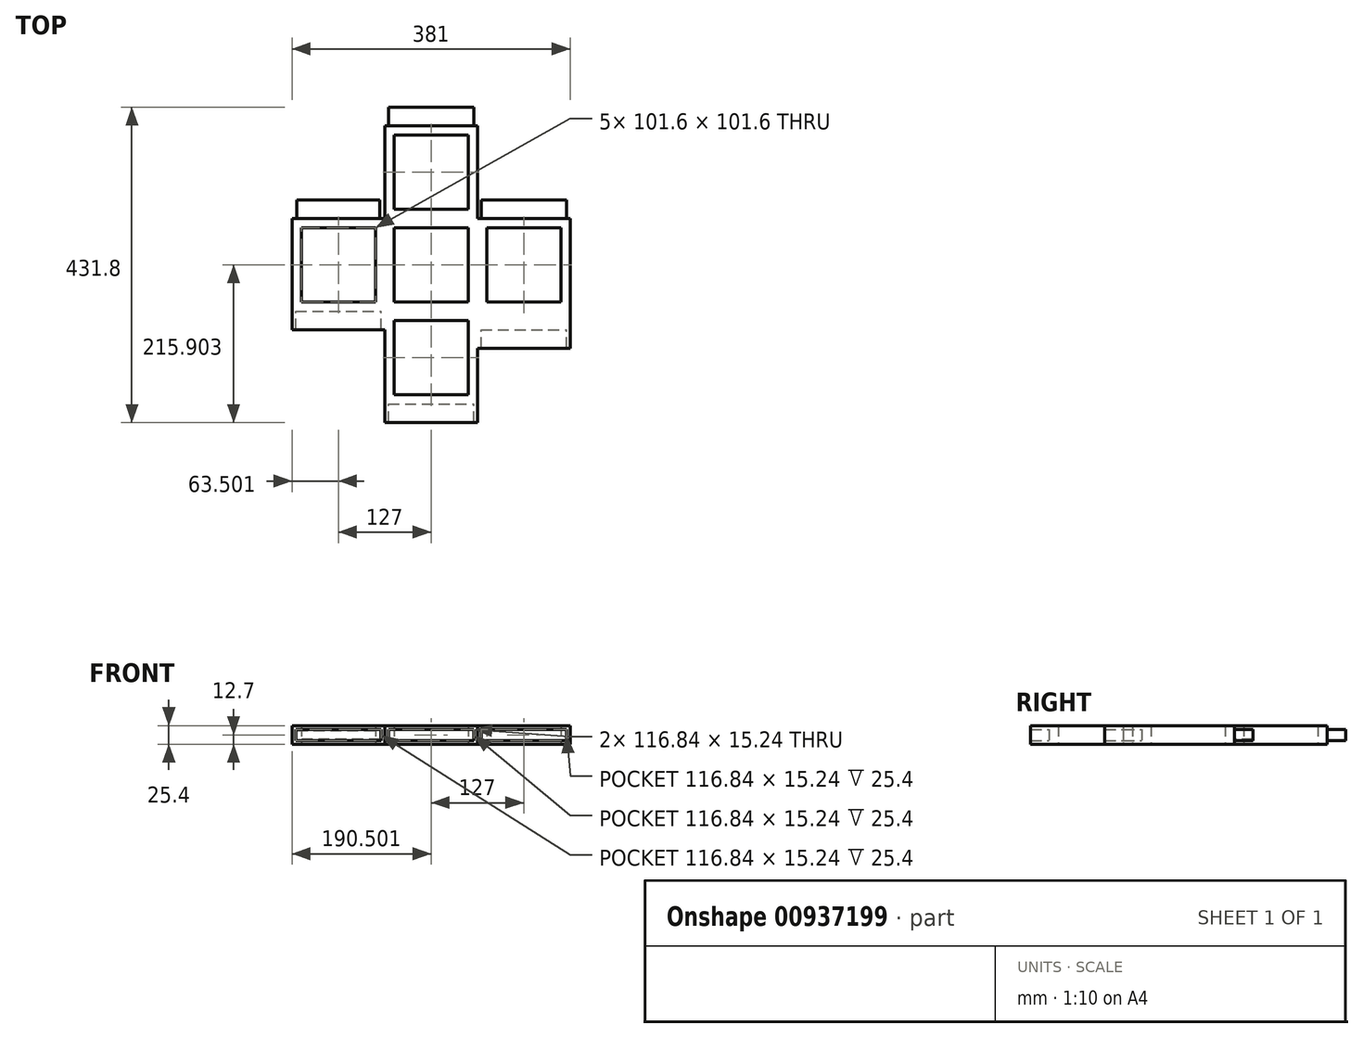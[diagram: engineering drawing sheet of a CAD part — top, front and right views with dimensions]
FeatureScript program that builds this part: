
annotation { "Feature Type Name" : "Feature", "Feature Type Description" : "" }
export const myFeature = defineFeature(function(context is Context, id is Id, definition is map)
    precondition{}
    {
        {
            var Q0;
            Q0=qCreatedBy(makeId("Top.planeOp"),FACE);
            var sketch = newSketch(context, id + "F0", { "sketchPlane" : qUnion([Q0])});
            skLineSegment(sketch, "E0.bottom", {"start": v(-63.69, 63.92) * mm, "end": v(63.31, 63.92) * mm});
            skLineSegment(sketch, "E0.top", {"start": v(-63.69, -63.08) * mm, "end": v(63.31, -63.08) * mm});
            skLineSegment(sketch, "E0.left", {"start": v(-63.69, 63.92) * mm, "end": v(-63.69, -63.08) * mm});
            skLineSegment(sketch, "E0.right", {"start": v(63.31, 63.92) * mm, "end": v(63.31, -63.08) * mm});
            skPoint(sketch, "E1", {"position": v(0, 0) * mm});
            skLineSegment(sketch, "E2", {"start": v(-63.69, 63.92) * mm, "end": v(63.31, -63.08) * mm, "construction": true});
            skLineSegment(sketch, "E3", {"start": v(63.31, 63.92) * mm, "end": v(-63.69, -63.08) * mm, "construction": true});
            skLineSegment(sketch, "E4.0", {"start": v(-50.99, 51.22) * mm, "end": v(50.61, 51.22) * mm});
            skLineSegment(sketch, "E4.1", {"start": v(-50.99, 51.22) * mm, "end": v(-50.99, -50.38) * mm});
            skLineSegment(sketch, "E4.2", {"start": v(-50.99, -50.38) * mm, "end": v(50.61, -50.38) * mm});
            skLineSegment(sketch, "E4.3", {"start": v(50.61, 51.22) * mm, "end": v(50.61, -50.38) * mm});
            skPoint(sketch, "E5.MirrorP", {"position": v(126.62, 0) * mm});
            skLineSegment(sketch, "E6.MirrorCS", {"start": v(190.31, 63.92) * mm, "end": v(190.31, -63.08) * mm});
            skLineSegment(sketch, "E7.MirrorCS", {"start": v(177.61, 51.22) * mm, "end": v(76.01, 51.22) * mm});
            skLineSegment(sketch, "E8.MirrorCS", {"start": v(76.01, 51.22) * mm, "end": v(76.01, -50.38) * mm});
            skLineSegment(sketch, "E9.MirrorCS", {"start": v(177.61, 51.22) * mm, "end": v(177.61, -50.38) * mm});
            skLineSegment(sketch, "E10.MirrorCS", {"start": v(177.61, -50.38) * mm, "end": v(76.01, -50.38) * mm});
            skLineSegment(sketch, "E11.MirrorCS", {"start": v(190.31, -63.08) * mm, "end": v(63.31, -63.08) * mm});
            skPoint(sketch, "E12.MirrorP", {"position": v(0, -126.15) * mm});
            skLineSegment(sketch, "E13.MirrorCS", {"start": v(50.61, -177.38) * mm, "end": v(50.61, -75.78) * mm});
            skLineSegment(sketch, "E14.MirrorCS", {"start": v(-50.99, -75.78) * mm, "end": v(50.61, -75.78) * mm});
            skLineSegment(sketch, "E15.MirrorCS", {"start": v(-50.99, -177.38) * mm, "end": v(-50.99, -75.78) * mm});
            skLineSegment(sketch, "E16.MirrorCS", {"start": v(-50.99, -177.38) * mm, "end": v(50.61, -177.38) * mm});
            skPoint(sketch, "E17.MirrorP", {"position": v(-127.38, 0) * mm});
            skLineSegment(sketch, "E18.MirrorCS", {"start": v(-76.39, 51.22) * mm, "end": v(-76.39, -50.38) * mm});
            skLineSegment(sketch, "E19.MirrorCS", {"start": v(-177.99, 51.22) * mm, "end": v(-177.99, -50.38) * mm});
            skLineSegment(sketch, "E20.MirrorCS", {"start": v(-76.39, -50.38) * mm, "end": v(-177.99, -50.38) * mm});
            skLineSegment(sketch, "E21.MirrorCS", {"start": v(-76.39, 51.22) * mm, "end": v(-177.99, 51.22) * mm});
            skLineSegment(sketch, "E22.MirrorCS", {"start": v(-63.69, 63.92) * mm, "end": v(-190.69, 63.92) * mm});
            skPoint(sketch, "E23.MirrorP", {"position": v(0, 127.85) * mm});
            skLineSegment(sketch, "E24.MirrorCS", {"start": v(50.61, 76.62) * mm, "end": v(50.61, 178.22) * mm});
            skLineSegment(sketch, "E25.MirrorCS", {"start": v(-50.99, 76.62) * mm, "end": v(-50.99, 178.22) * mm});
            skLineSegment(sketch, "E26.MirrorCS", {"start": v(-50.99, 178.22) * mm, "end": v(50.61, 178.22) * mm});
            skLineSegment(sketch, "E27.MirrorCS", {"start": v(-50.99, 76.62) * mm, "end": v(50.61, 76.62) * mm});
            skLineSegment(sketch, "E28", {"start": v(-190.69, 63.92) * mm, "end": v(-190.69, -63.08) * mm});
            skLineSegment(sketch, "E29", {"start": v(-63.69, -63.08) * mm, "end": v(-190.69, -63.08) * mm});
            skLineSegment(sketch, "E30", {"start": v(63.31, 63.92) * mm, "end": v(190.31, 63.92) * mm});
            skLineSegment(sketch, "E31", {"start": v(-63.69, -63.08) * mm, "end": v(-63.69, -190.08) * mm});
            skLineSegment(sketch, "E32", {"start": v(63.31, -190.08) * mm, "end": v(-63.69, -190.08) * mm});
            skLineSegment(sketch, "E33", {"start": v(63.31, -190.08) * mm, "end": v(63.31, -63.08) * mm});
            skLineSegment(sketch, "E34", {"start": v(-63.69, 63.92) * mm, "end": v(-63.69, 190.92) * mm});
            skLineSegment(sketch, "E35", {"start": v(63.31, 190.92) * mm, "end": v(-63.69, 190.92) * mm});
            skLineSegment(sketch, "E36", {"start": v(63.31, 190.92) * mm, "end": v(63.31, 63.92) * mm});
            skSolve(sketch);
        }
        {
            var Q0;
            Q0 = qSketchRegion(id + "F0", true);
            extrude(context, id + "F1", {"entities" : qUnion([Q0]), "depth" : 25.4 * mm, "offsetDistance" : 25.4 * mm});
        }
        {
            var Q0;
            Q0=makeQuery(id+"F1.opExtrude","SWEPT_FACE",FACE,{"disambiguationData":[OSD([sQuery(id+"F0.wireOp",EDGE,"E35")])]});
            var sketch = newSketch(context, id + "F2", { "sketchPlane" : qUnion([Q0])});
            skLineSegment(sketch, "E37.0", {"start": v(-58.23, 5.08) * mm, "end": v(58.6, 5.08) * mm});
            skLineSegment(sketch, "E37.1", {"start": v(-58.23, 20.32) * mm, "end": v(-58.23, 5.08) * mm});
            skLineSegment(sketch, "E37.2", {"start": v(58.6, 20.32) * mm, "end": v(-58.23, 20.32) * mm});
            skLineSegment(sketch, "E37.3", {"start": v(58.6, 5.08) * mm, "end": v(58.6, 20.32) * mm});
            skLineSegment(sketch, "E38.0", {"start": v(-63.31, 20.32) * mm, "end": v(-63.31, 5.08) * mm});
            skSolve(sketch);
        }
        {
            var Q0;
            Q0=makeQuery(id+"F2.imprint","IMPRINT",FACE,{"disambiguationData":[TD([[makeQuery(id+"F2.imprint","IMPRINT",EDGE,{"derivedFrom":sQuery(id+"F2.wireOp",EDGE,"E37.0")}),1.0]])]});
            extrude(context, id + "F3", {"entities" : qUnion([Q0]), "operationType" : NewBodyOperationType.ADD, "depth" : 25.4 * mm, "offsetDistance" : 25.4 * mm});
        }
        {
            var Q0;
            Q0=makeQuery(id+"F1.opExtrude","SWEPT_FACE",FACE,{"disambiguationData":[OSD([sQuery(id+"F0.wireOp",EDGE,"E22.MirrorCS")])]});
            var sketch = newSketch(context, id + "F4", { "sketchPlane" : qUnion([Q0])});
            skSolve(sketch);
        }
        {
            var Q0;
            {var subQ0=sQuery(id+"F0.wireOp",EDGE,"E22.MirrorCS");Q0=makeQuery(id+"F4.imprint","IMPRINT",FACE,{"disambiguationData":[TD([[makeQuery(id+"F4.imprint","IMPRINT",EDGE,{"derivedFrom":makeQuery(id+"F1.opExtrude","CAP_EDGE",EDGE,{"disambiguationData":[OSD([subQ0])],"isStart":true})}),1.0]])]});}
            var sketch = newSketch(context, id + "F5", { "sketchPlane" : qUnion([Q0])});
            skLineSegment(sketch, "E39.0", {"start": v(70.35, 18.74) * mm, "end": v(70.35, 6.66) * mm});
            skLineSegment(sketch, "E39.1", {"start": v(184.03, 18.74) * mm, "end": v(70.35, 18.74) * mm});
            skLineSegment(sketch, "E39.2", {"start": v(184.03, 6.66) * mm, "end": v(184.03, 18.74) * mm});
            skLineSegment(sketch, "E39.3", {"start": v(70.35, 6.66) * mm, "end": v(184.03, 6.66) * mm});
            skSolve(sketch);
        }
        {
            var Q0;
            Q0=makeQuery(id+"F5.imprint","IMPRINT",FACE,{"disambiguationData":[TD([[makeQuery(id+"F5.imprint","IMPRINT",EDGE,{"derivedFrom":sQuery(id+"F5.wireOp",EDGE,"E39.0")}),1.0]])]});
            extrude(context, id + "F6", {"entities" : qUnion([Q0]), "operationType" : NewBodyOperationType.ADD, "depth" : 25.4 * mm, "offsetDistance" : 25.4 * mm});
        }
        {
            var Q0;
            Q0=makeQuery(id+"F1.opExtrude","SWEPT_FACE",FACE,{"disambiguationData":[OSD([sQuery(id+"F0.wireOp",EDGE,"E30")])]});
            var sketch = newSketch(context, id + "F7", { "sketchPlane" : qUnion([Q0])});
            skLineSegment(sketch, "E40.0", {"start": v(-185.23, 5.08) * mm, "end": v(-68.4, 5.08) * mm});
            skLineSegment(sketch, "E40.1", {"start": v(-185.23, 20.32) * mm, "end": v(-185.23, 5.08) * mm});
            skLineSegment(sketch, "E40.2", {"start": v(-68.4, 20.32) * mm, "end": v(-185.23, 20.32) * mm});
            skLineSegment(sketch, "E40.3", {"start": v(-68.4, 5.08) * mm, "end": v(-68.4, 20.32) * mm});
            skLineSegment(sketch, "E41.0", {"start": v(-180.15, 20.32) * mm, "end": v(-180.15, 5.08) * mm});
            skSolve(sketch);
        }
        {
            var Q0;
            {var subQ0=sQuery(id+"F7.wireOp",EDGE,"E40.1");Q0=makeQuery(id+"F7.imprint","IMPRINT",FACE,{"disambiguationData":[TD([[makeQuery(id+"F7.imprint","IMPRINT",EDGE,{"derivedFrom":subQ0}),1.0]])]});}
            var Q1;
            {var subQ0=sQuery(id+"F7.wireOp",EDGE,"E40.3");Q1=makeQuery(id+"F7.imprint","IMPRINT",FACE,{"disambiguationData":[TD([[makeQuery(id+"F7.imprint","IMPRINT",EDGE,{"derivedFrom":subQ0}),1.0]])]});}
            extrude(context, id + "F8", {"entities" : qUnion([Q0, Q1]), "operationType" : NewBodyOperationType.ADD, "depth" : 25.4 * mm, "offsetDistance" : 25.4 * mm});
        }
        {
            var Q0;
            Q0=makeQuery(id+"F1.opExtrude","SWEPT_FACE",FACE,{"disambiguationData":[OSD([sQuery(id+"F0.wireOp",EDGE,"E11.MirrorCS")])]});
            var sketch = newSketch(context, id + "F9", { "sketchPlane" : qUnion([Q0])});
            skLineSegment(sketch, "E42.0", {"start": v(68.4, 5.08) * mm, "end": v(185.23, 5.08) * mm});
            skLineSegment(sketch, "E42.1", {"start": v(68.4, 20.32) * mm, "end": v(68.4, 5.08) * mm});
            skLineSegment(sketch, "E42.2", {"start": v(185.23, 20.32) * mm, "end": v(68.4, 20.32) * mm});
            skLineSegment(sketch, "E42.3", {"start": v(185.23, 5.08) * mm, "end": v(185.23, 20.32) * mm});
            skSolve(sketch);
        }
        {
            var Q0;
            Q0 = qSketchRegion(id + "F9", true);
            var Q1;
            Q1=makeQuery(id+"F9.imprint","IMPRINT",FACE,{"disambiguationData":[TD([[makeQuery(id+"F9.imprint","IMPRINT",EDGE,{"derivedFrom":sQuery(id+"F9.wireOp",EDGE,"E42.0")}),-1.0]])]});
            extrude(context, id + "F10", {"entities" : qUnion([Q0, Q1]), "operationType" : NewBodyOperationType.ADD, "depth" : 25.4 * mm, "offsetDistance" : 25.4 * mm});
        }
        {
            var Q0;
            Q0=makeQuery(id+"F10.opExtrude","CAP_FACE",FACE,{"disambiguationData":[OSD([sQuery(id+"F0.wireOp",EDGE,"E0.top"),sQuery(id+"F0.wireOp",EDGE,"E0.right"),sQuery(id+"F0.wireOp",EDGE,"E6.MirrorCS"),sQuery(id+"F0.wireOp",EDGE,"E11.MirrorCS"),sQuery(id+"F0.wireOp",EDGE,"E33")])],"isStart":false});
            var sketch = newSketch(context, id + "F11", { "sketchPlane" : qUnion([Q0])});
            skLineSegment(sketch, "E43.0", {"start": v(68.4, 5.08) * mm, "end": v(185.23, 5.08) * mm});
            skLineSegment(sketch, "E43.1", {"start": v(68.4, 20.32) * mm, "end": v(68.4, 5.08) * mm});
            skLineSegment(sketch, "E43.2", {"start": v(185.23, 20.32) * mm, "end": v(68.4, 20.32) * mm});
            skLineSegment(sketch, "E43.3", {"start": v(185.23, 5.08) * mm, "end": v(185.23, 20.32) * mm});
            skSolve(sketch);
        }
        {
            var Q0;
            Q0=makeQuery(id+"F11.imprint","IMPRINT",FACE,{"disambiguationData":[TD([[makeQuery(id+"F11.imprint","IMPRINT",EDGE,{"derivedFrom":sQuery(id+"F11.wireOp",EDGE,"E43.0")}),-1.0]])]});
            extrude(context, id + "F12", {"entities" : qUnion([Q0]), "operationType" : NewBodyOperationType.ADD, "depth" : 25.4 * mm, "offsetDistance" : 25.4 * mm});
        }
        {
            var Q0;
            Q0=makeQuery(id+"F1.opExtrude","SWEPT_FACE",FACE,{"disambiguationData":[OSD([sQuery(id+"F0.wireOp",EDGE,"E32")])]});
            var sketch = newSketch(context, id + "F13", { "sketchPlane" : qUnion([Q0])});
            skLineSegment(sketch, "E44.0", {"start": v(-58.6, 5.08) * mm, "end": v(58.23, 5.08) * mm});
            skLineSegment(sketch, "E44.1", {"start": v(-58.6, 20.32) * mm, "end": v(-58.6, 5.08) * mm});
            skLineSegment(sketch, "E44.2", {"start": v(58.23, 20.32) * mm, "end": v(-58.6, 20.32) * mm});
            skLineSegment(sketch, "E44.3", {"start": v(58.23, 5.08) * mm, "end": v(58.23, 20.32) * mm});
            skSolve(sketch);
        }
        {
            var Q0;
            Q0=makeQuery(id+"F13.imprint","IMPRINT",FACE,{"disambiguationData":[TD([[makeQuery(id+"F13.imprint","IMPRINT",EDGE,{"derivedFrom":sQuery(id+"F13.wireOp",EDGE,"E44.0")}),-1.0]])]});
            extrude(context, id + "F14", {"entities" : qUnion([Q0]), "operationType" : NewBodyOperationType.ADD, "depth" : 25.4 * mm, "offsetDistance" : 25.4 * mm});
        }
        {
            var Q0;
            Q0=makeQuery(id+"F1.opExtrude","SWEPT_FACE",FACE,{"disambiguationData":[OSD([sQuery(id+"F0.wireOp",EDGE,"E29")])]});
            var sketch = newSketch(context, id + "F15", { "sketchPlane" : qUnion([Q0])});
            skLineSegment(sketch, "E45.0", {"start": v(-185.6, 5.08) * mm, "end": v(-68.77, 5.08) * mm});
            skLineSegment(sketch, "E45.1", {"start": v(-185.6, 20.32) * mm, "end": v(-185.6, 5.08) * mm});
            skLineSegment(sketch, "E45.2", {"start": v(-68.77, 20.32) * mm, "end": v(-185.6, 20.32) * mm});
            skLineSegment(sketch, "E45.3", {"start": v(-68.77, 5.08) * mm, "end": v(-68.77, 20.32) * mm});
            skSolve(sketch);
        }
        {
            var Q0;
            Q0=makeQuery(id+"F15.imprint","IMPRINT",FACE,{"disambiguationData":[TD([[makeQuery(id+"F15.imprint","IMPRINT",EDGE,{"derivedFrom":sQuery(id+"F15.wireOp",EDGE,"E45.0")}),-1.0]])]});
            extrude(context, id + "F16", {"entities" : qUnion([Q0]), "operationType" : NewBodyOperationType.ADD, "depth" : 25.4 * mm, "offsetDistance" : 25.4 * mm});
        }
    });
